# Revit family: Gira_039800
name_source: partatom
category: Allgemeines Modell
revit_build: Autodesk Revit 2017 (Build: 20160225_1515(x64)
units: mm (PartAtom-declared; Revit-internal decimal feet)

## family parameters
Basisbauteil = Fläche
Beim Laden mit Abzugskörper schneiden = Nein
Bemaßung runder Anschluss = Durchmesser verwenden
Gemeinsam genutzt = Nein
Kann Basisbauteil für Bewehrung sein = Nein
Raumberechnungspunkt = Nein
Teiletyp = Normal

## types (1)
- Gira_039800
    Assembly arrangement = Basic element
    BIM = https://media.stage.bim.site
    Beschreibung = Blind cont.230V aux.in. Ins.,Blind controller insert 230 V~ with auxiliary input,,,Features:,Can be set with eNet server.:,- Localisation of the device.,- Fully encrypted wireless transmission (AES CCM) from eNet Server software version 2.0.,- Operation locks.,- Device software update.,- Control of a blind or shutter motor with mechanical or electronic end-position switches.,- Mechanical buttons or additional blind controller inserts which can be connected via 230 V auxiliary inputs for establishing group controls.,- Wind alarm function" can be realised using auxiliary inputs.,- Motor protection using mutually interlocked relay contacts with a minimum changeover time.,,Notes :,- The range can be reduced when using a metal top unit and or metal cover frames.,- Wireless approval is valid for EU and EFTA countries.,- N conductor required.,- Using a deep device box is recommended."
    Colour = Other
    Data sheet = https://katalog.gira.de
    GTIN = 4010337398004
    HAN = 039800
    Halogen free = Nein
    Hersteller = Gira
    Integrated timer = Nein
    Material = Other
    Material quality = Other
    Max. switching power [Voltampere] = 1000
    Mounting method = Flush mounted (plaster)
    Nominal voltage [Volt] = 230
    Productwebsite = http://katalog.gira.de
    Random generator = Nein
    Substation input = Ja
    Suitable for degree of protection (IP) = IP20
    Suitable for rain sensor = Nein
    Suitable for wind sensor = Nein
    Surface finishing = Not applicable
    Surface protection = Other
    Switch-off protection = Nein
    Transparent = Nein
    Type of fastening = Mounting with claw and screw
    Typname = Blind cont. 230 V + aux.input Insert
    URL = https://www.gira.de
    Vorgabe-Ansicht = 1219 mm
    With Astro program = Nein
    With brightness sensor connection = Nein
    With glass breaking detector connection = Nein
    With memory function = Nein

## geometry (parser evidence)
native form markers: Sweep x2
no freeform markers — native parametric forms only
